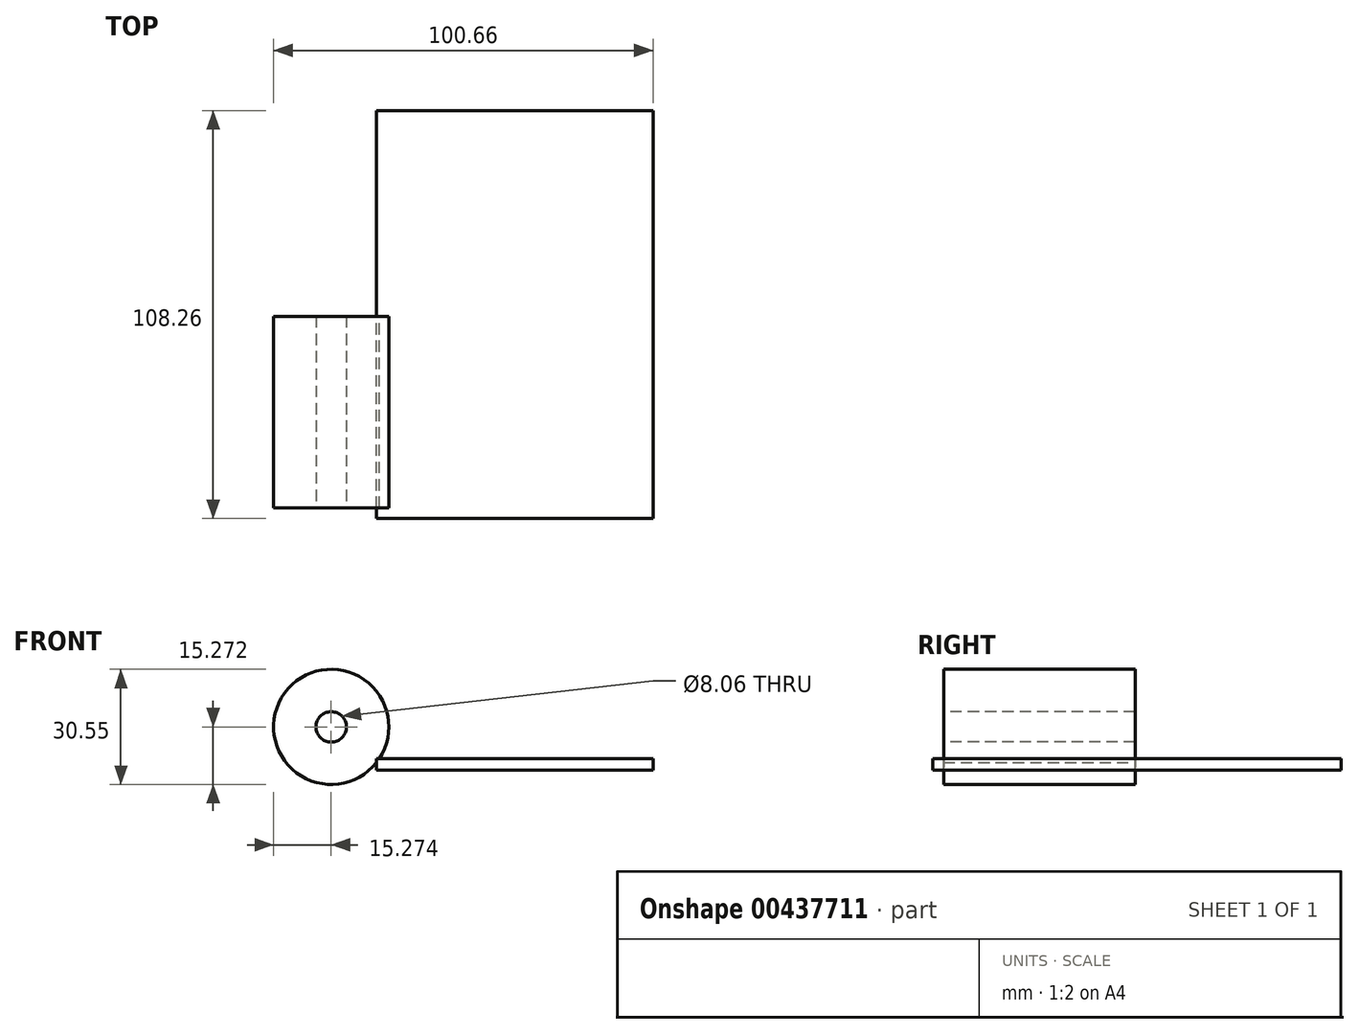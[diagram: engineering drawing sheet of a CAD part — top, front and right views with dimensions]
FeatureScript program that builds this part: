
annotation { "Feature Type Name" : "Feature", "Feature Type Description" : "" }
export const myFeature = defineFeature(function(context is Context, id is Id, definition is map)
    precondition{}
    {
        {
            var Q0;
            Q0=qCreatedBy(makeId("Top.planeOp"),FACE);
            var sketch = newSketch(context, id + "F0", { "sketchPlane" : qUnion([Q0])});
            skLineSegment(sketch, "E0.bottom", {"start": v(-5.57, -53.66) * mm, "end": v(67.83, -53.66) * mm});
            skLineSegment(sketch, "E0.top", {"start": v(-5.57, 54.6) * mm, "end": v(67.83, 54.6) * mm});
            skLineSegment(sketch, "E0.left", {"start": v(-5.57, -53.66) * mm, "end": v(-5.57, 54.6) * mm});
            skLineSegment(sketch, "E0.right", {"start": v(67.83, -53.66) * mm, "end": v(67.83, 54.6) * mm});
            skSolve(sketch);
        }
        {
            var Q0;
            Q0=makeQuery(id+"F0.imprint","IMPRINT",FACE,{"disambiguationData":[TD([[makeQuery(id+"F0.imprint","IMPRINT",EDGE,{"derivedFrom":sQuery(id+"F0.wireOp",EDGE,"E0.bottom")}),1.0]])]});
            extrude(context, id + "F1", {"entities" : qUnion([Q0]), "depth" : 3.05 * mm});
        }
        {
            var Q0;
            Q0=qCreatedBy(makeId("Front.planeOp"),FACE);
            var sketch = newSketch(context, id + "F2", { "sketchPlane" : qUnion([Q0])});
            skCircle(sketch, "E1", {"center": v(-17.56, 11.51) * mm, "radius": 15.28 * mm});
            skSolve(sketch);
        }
        {
            var Q0;
            Q0=makeQuery(id+"F2.imprint","IMPRINT",FACE,{"disambiguationData":[TD([[makeQuery(id+"F2.imprint","IMPRINT",EDGE,{"derivedFrom":sQuery(id+"F2.wireOp",EDGE,"E1")}),1.0]])]});
            extrude(context, id + "F3", {"entities" : qUnion([Q0]), "operationType" : NewBodyOperationType.ADD, "depth" : 50.8 * mm});
        }
        {
            var Q0;
            Q0=makeQuery(id+"F3.opExtrude","CAP_FACE",FACE,{"disambiguationData":[OSD([sQuery(id+"F2.wireOp",EDGE,"E1")])],"isStart":false});
            var sketch = newSketch(context, id + "F4", { "sketchPlane" : qUnion([Q0])});
            skCircle(sketch, "E2", {"center": v(-17.56, 11.51) * mm, "radius": 4.03 * mm});
            skSolve(sketch);
        }
        {
            var Q0;
            Q0=makeQuery(id+"F4.imprint","IMPRINT",FACE,{"disambiguationData":[TD([[makeQuery(id+"F4.imprint","IMPRINT",EDGE,{"derivedFrom":sQuery(id+"F4.wireOp",EDGE,"E2")}),1.0]])]});
            var Q1;
            Q1=sQuery(id+"F4.wireOp",EDGE,"E2");
            extrude(context, id + "F5", {"entities" : qUnion([Q0]), "operationType" : NewBodyOperationType.REMOVE, "surfaceEntities" : qUnion([Q1]), "oppositeDirection" : true, "depth" : 50.8 * mm});
        }
    });
